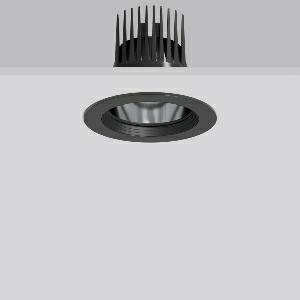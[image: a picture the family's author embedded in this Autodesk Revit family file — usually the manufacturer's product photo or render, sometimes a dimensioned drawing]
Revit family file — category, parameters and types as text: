
# Revit family: heledon_maxi_e_901766_003_3_76_2c52
name_source: partatom
category: Lighting Fixtures
units: mm (PartAtom-declared; Revit-internal decimal feet)

## family parameters
Cut with Voids When Loaded = No
Host = Face
Light Source = No
Part Type = Normal
Room Calculation Point = No
Round Connector Dimension = Use Diameter
Shared = No

## types (1)
- HELEDON maxi E (1 x LED Modul 935, 4200 lm, 3500)
    Apparent Load = 35 VA
    Approval mark = CE
    CIE Flux Codes = 97 100 100 100 100
    Color Rendering = 92
    Color Temperature = 3500
    Default Elevation = 1800 mm
    Description = Series: HELEDON maxi
Round recessed downlight. Housing: die-cast aluminium, powder-coated. Black plastic ring and recessed LED to prevent glare from the side. Optical assembly with reflector made of MIRO-Silver with 98% total light reflection for outstanding efficiency - can be changed without tools. Best colour rendering index Ra>90. Suitable for Recessed ceiling mounting. Installation without tools thanks to spring fastening system. Including separate LED converter with connecting cable 600 mm.High quality converter without flickering and stroboscopic effect. Through-wiring box (5 pole) available as accessory. The following accessories can be mounted without use of tools: interchangeable lenses, decorative glasses, honeycomb louvre, clear and frosted diffusers, white interchangeable plastic ring. 
Colour: deep black, matt (RAL 9005)
Diameter: 162 mm
Height: 3 mm
Cut-out diameter: 152 mm
Recess height: 200 mm
Luminaire: recess height: 135 mm
Lamp: LED
Socket: without socket
Colour temperature: 3500K
Colour rendering index (CRI): 92
System power: 35 W
Rated luminous flux: 4200 lm
Luminous efficiency: 120 lm/W
Control gear: Converter, dimmable, DALI
Protection class: II
Type of protection: IP 20
    Height = 0 mm  [stored 0 ft]
    Lamp = 1 x LED Modul 935
    Lamp Light Flux = 4200 lm
    Lamp count = 1
    Length = 162 mm
    Lifetime = 50000 h
    Luminous efficacy = 120 lm/W
    Manufacturer = RZB
    ModVariant = No
    Model = 901766.003.3.76
    Mounting Place = Ceiling
    Mounting Type = Recessed
    Number of Poles = 1
    OnlyDefault = Yes
    Power Factor = 1
    Product Name = HELEDON maxi E
    Product group = Recessed downlights
    ProductGroupID = 402
    Protection Class = Protection class II
    Protection Degree = IP 20
    RLX_Detail_Level = 1
    RLX_Emergency_Light_Flux = 0 lm
    RLX_Emergency_Type = 0
    RLX_Emergency_Type_DB = No
    RlxData = <blob elided: 121449 chars, md5=caf528ef>
    Socket = socket
    Standby Power = 0 W
    System Light Flux = 4200 lm
    System Power = 35 W
    Type Comments = Product without accessories
    Type Image = 901662.003.jpg
    URL = http://relux.com
    VarID = ---
    Voltage = 230 V
    Voltage Range = 220-240 V
    Weight = 0.00 kg
    Width = 0 mm  [stored 0 ft]

note: [stored X ft] marks values corroborated as IEEE doubles in the binary element streams (Revit-internal decimal feet)

## geometry (parser evidence)
native form markers: Blend x4, Sweep x12
no freeform markers — native parametric forms only
